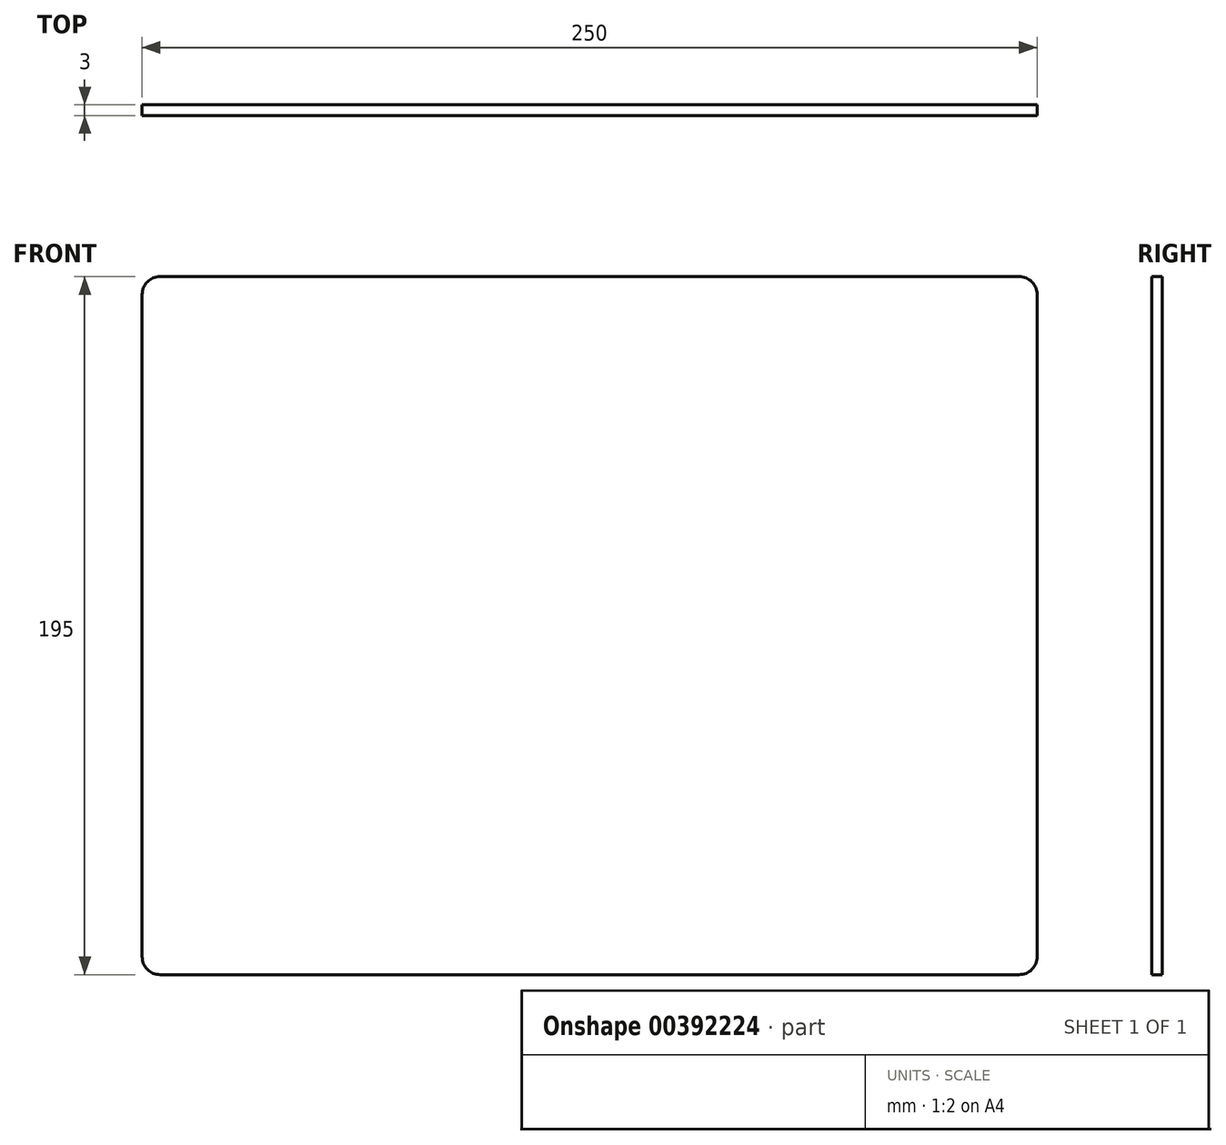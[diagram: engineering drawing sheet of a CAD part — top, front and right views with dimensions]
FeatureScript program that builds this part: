
annotation { "Feature Type Name" : "Feature", "Feature Type Description" : "" }
export const myFeature = defineFeature(function(context is Context, id is Id, definition is map)
    precondition{}
    {
        {
            var Q0;
            Q0=qCreatedBy(makeId("Front.planeOp"),FACE);
            var sketch = newSketch(context, id + "F0", { "sketchPlane" : qUnion([Q0])});
            skLineSegment(sketch, "E0.bottom", {"start": v(5, 0) * mm, "end": v(245, 0) * mm});
            skLineSegment(sketch, "E0.top", {"start": v(5, 195) * mm, "end": v(245, 195) * mm});
            skLineSegment(sketch, "E0.left", {"start": v(0, 5) * mm, "end": v(0, 190) * mm});
            skLineSegment(sketch, "E0.right", {"start": v(250, 5) * mm, "end": v(250, 190) * mm});
            skPoint(sketch, "E1.visualSharp", {"position": v(0, 195) * mm});
            skArc(sketch, "E1.filletArc", {"start": v(5, 195) * mm, "mid": v(1.46, 193.54) * mm, "end": v(0, 190) * mm});
            skPoint(sketch, "E2.visualSharp", {"position": v(0, 0) * mm});
            skArc(sketch, "E2.filletArc", {"start": v(0, 5) * mm, "mid": v(1.46, 1.46) * mm, "end": v(5, 0) * mm});
            skPoint(sketch, "E3.visualSharp", {"position": v(250, 0) * mm});
            skArc(sketch, "E3.filletArc", {"start": v(245, 0) * mm, "mid": v(248.54, 1.46) * mm, "end": v(250, 5) * mm});
            skPoint(sketch, "E4.visualSharp", {"position": v(250, 195) * mm});
            skArc(sketch, "E4.filletArc", {"start": v(250, 190) * mm, "mid": v(248.54, 193.54) * mm, "end": v(245, 195) * mm});
            skSolve(sketch);
        }
        {
            var Q0;
            Q0=makeQuery(id+"F0.imprint","IMPRINT",FACE,{"disambiguationData":[TD([[makeQuery(id+"F0.imprint","IMPRINT",EDGE,{"derivedFrom":sQuery(id+"F0.wireOp",EDGE,"E0.bottom")}),1.0]])]});
            extrude(context, id + "F1", {"entities" : qUnion([Q0]), "depth" : 3 * mm});
        }
    });
